# Revit family: НЕВАТОМ_Узел прохода УП3-2, версия 1
name_source: partatom
category: Арматура воздуховодов
revit_build: Autodesk Revit 2017 (Build: 20170118_1100(x64)
units: mm (PartAtom-declared; Revit-internal decimal feet)

## family parameters
Всегда вертикально = Да
На основе рабочей плоскости = Нет
Общий = Нет
При загрузке вырезать с полостями = Нет
Размер круглого соединителя = Использовать диаметр
Тип детали = Вставляется

## types (16) — shared parameters
130 = 130 мм
ADSK_Единица измерения = шт.
ADSK_Завод-изготовитель = НЕВАТОМ
ADSK_Количество = 1
ADSK_Материал наименование = Черная сталь
ADSK_Напряжение = 0 В
ADSK_Полная мощность = 0 В·А
ADSK_Размер_Высота = 1130 мм
ADSK_Ток = 0 А
H = 200 мм
L = 1000 мм
Nevatom_URL = https://t.me
t = 3 мм

## per-type parameters (varying)
| type | ADSK_Размер_Длина | ADSK_Размер_Ширина | D | D+3 | D1 | D2 наруж. опорного к. | Df наружн. фланц. | Df1 | d1 |
| УЗЕЛ ПРОХОДА-УП3-2-0-200-1000 | 540 мм | 540 мм | 200 мм | 203 мм | 540 мм | 540 мм | 269 мм | 230 мм | 520 мм |
| УЗЕЛ ПРОХОДА-УП3-2-0-250-1000 | 540 мм | 540 мм | 250 мм | 253 мм | 540 мм | 540 мм | 319 мм | 280 мм | 515 мм |
| УЗЕЛ ПРОХОДА-УП3-2-0-280-1000 | 540 мм | 540 мм | 280 мм | 283 мм | 540 мм | 540 мм | 349 мм | 310 мм | 512 мм |
| УЗЕЛ ПРОХОДА-УП3-2-0-315-1000 | 690 мм | 690 мм | 315 мм | 318 мм | 690 мм | 690 мм | 384 мм | 345 мм | 659 мм |
| УЗЕЛ ПРОХОДА-УП3-2-0-355-1000 | 690 мм | 690 мм | 355 мм | 358 мм | 690 мм | 690 мм | 414 мм | 380 мм | 655 мм |
| УЗЕЛ ПРОХОДА-УП3-2-0-400-1000 | 840 мм | 840 мм | 400 мм | 403 мм | 840 мм | 840 мм | 459 мм | 425 мм | 800 мм |
| УЗЕЛ ПРОХОДА-УП3-2-0-450-1000 | 840 мм | 840 мм | 450 мм | 453 мм | 840 мм | 840 мм | 509 мм | 475 мм | 795 мм |
| УЗЕЛ ПРОХОДА-УП3-2-0-500-1000 | 840 мм | 840 мм | 500 мм | 503 мм | 840 мм | 840 мм | 559 мм | 525 мм | 790 мм |
| УЗЕЛ ПРОХОДА-УП3-2-0-560-1000 | 840 мм | 840 мм | 560 мм | 563 мм | 840 мм | 840 мм | 619 мм | 585 мм | 784 мм |
| УЗЕЛ ПРОХОДА-УП3-2-0-630-1000 | 1140 мм | 1140 мм | 630 мм | 633 мм | 1140 мм | 1140 мм | 689 мм | 655 мм | 1077 мм |
| УЗЕЛ ПРОХОДА-УП3-2-0-710-1000 | 1140 мм | 1140 мм | 710 мм | 713 мм | 1140 мм | 1140 мм | 783 мм | 742 мм | 1069 мм |
| УЗЕЛ ПРОХОДА-УП3-2-0-800-1000 | 1140 мм | 1140 мм | 800 мм | 803 мм | 1140 мм | 1140 мм | 873 мм | 832 мм | 1060 мм |
| УЗЕЛ ПРОХОДА-УП3-2-0-900-1000 | 1220 мм | 1220 мм | 900 мм | 903 мм | 1220 мм | 1220 мм | 973 мм | 932 мм | 1130 мм |
| УЗЕЛ ПРОХОДА-УП3-2-0-1000-1000 | 1340 мм | 1340 мм | 1000 мм | 1003 мм | 1340 мм | 1340 мм | 1073 мм | 1032 мм | 1240 мм |
| УЗЕЛ ПРОХОДА-УП3-2-0-1120-1000 | 1450 мм | 1450 мм | 1120 мм | 1123 мм | 1450 мм | 1450 мм | 1193 мм | 1152 мм | 1338 мм |
| УЗЕЛ ПРОХОДА-УП3-2-0-1250-1000 | 1590 мм | 1590 мм | 1250 мм | 1253 мм | 1590 мм | 1590 мм | 1323 мм | 1282 мм | 1465 мм |
